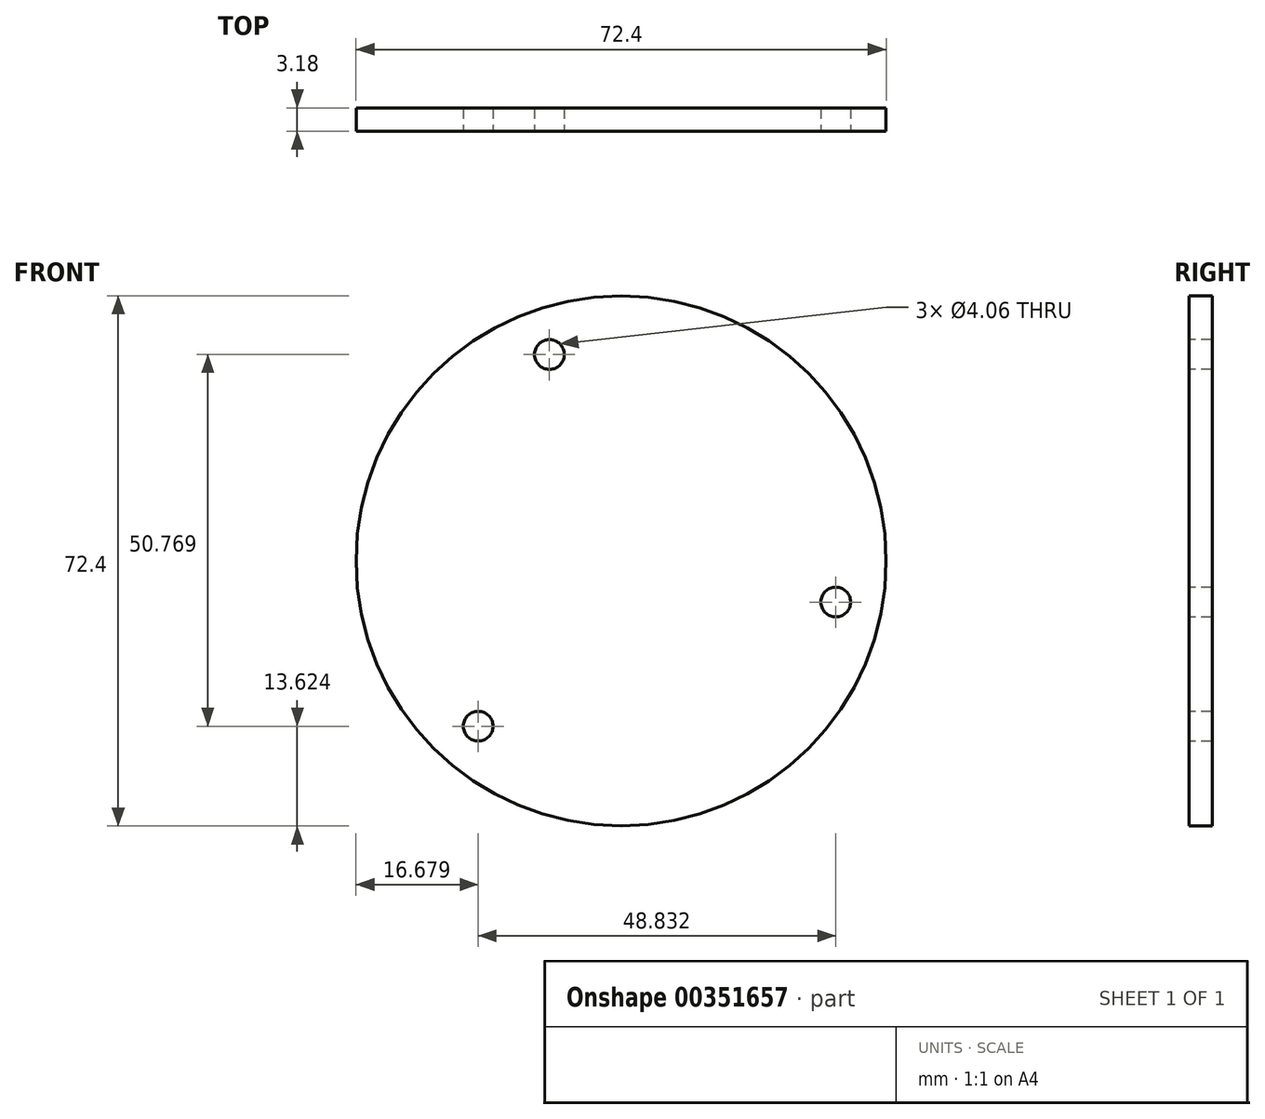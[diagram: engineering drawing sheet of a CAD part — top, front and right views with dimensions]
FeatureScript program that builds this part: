
annotation { "Feature Type Name" : "Feature", "Feature Type Description" : "" }
export const myFeature = defineFeature(function(context is Context, id is Id, definition is map)
    precondition{}
    {
        {
            var Q0;
            Q0=qCreatedBy(makeId("Front.planeOp"),FACE);
            var sketch = newSketch(context, id + "F0", { "sketchPlane" : qUnion([Q0])});
            skCircle(sketch, "E0", {"center": v(0, 0) * mm, "radius": 36.2 * mm});
            skSolve(sketch);
        }
        {
            var Q0;
            Q0=makeQuery(id+"F0.imprint","IMPRINT",FACE,{"disambiguationData":[TD([[makeQuery(id+"F0.imprint","IMPRINT",EDGE,{"derivedFrom":sQuery(id+"F0.wireOp",EDGE,"E0")}),1.0]])]});
            extrude(context, id + "F1", {"entities" : qUnion([Q0]), "depth" : 3.17 * mm});
        }
        {
            var Q0;
            Q0=makeQuery(id+"F1.opExtrude","CAP_FACE",FACE,{"disambiguationData":[OSD([sQuery(id+"F0.wireOp",EDGE,"E0")])],"isStart":false});
            var sketch = newSketch(context, id + "F2", { "sketchPlane" : qUnion([Q0])});
            skCircle(sketch, "E1", {"center": v(0, 0) * mm, "radius": 25.4 * mm, "construction": true});
            skCircle(sketch, "E2", {"center": v(-16.92, 18.95) * mm, "radius": 2.8 * mm});
            skCircle(sketch, "E3.1.0", {"center": v(-18.95, -16.92) * mm, "radius": 2.8 * mm});
            skCircle(sketch, "E3.2.0", {"center": v(16.92, -18.95) * mm, "radius": 2.8 * mm});
            skCircle(sketch, "E3.3.0", {"center": v(18.95, 16.92) * mm, "radius": 2.8 * mm});
            skSolve(sketch);
        }
        {
            var Q0;
            Q0=makeQuery(id+"F2.imprint","IMPRINT",FACE,{"disambiguationData":[TD([[makeQuery(id+"F2.imprint","IMPRINT",EDGE,{"derivedFrom":sQuery(id+"F2.wireOp",EDGE,"E2")}),-1.0]])]});
            var sketch = newSketch(context, id + "F3", { "sketchPlane" : qUnion([Q0])});
            skCircle(sketch, "E4", {"center": v(0, 0) * mm, "radius": 29.85 * mm, "construction": true});
            skCircle(sketch, "E5", {"center": v(-9.8, 28.2) * mm, "radius": 2.03 * mm});
            skCircle(sketch, "E6.1.0", {"center": v(-19.52, -22.58) * mm, "radius": 2.03 * mm});
            skCircle(sketch, "E6.2.0", {"center": v(29.31, -5.62) * mm, "radius": 2.03 * mm});
            skSolve(sketch);
        }
        {
            var Q0;
            Q0=qSketchRegion(id+"F3",true);
            extrude(context, id + "F4", {"entities" : qUnion([Q0]), "operationType" : NewBodyOperationType.REMOVE, "oppositeDirection" : true, "depth" : 25.4 * mm});
        }
    });
